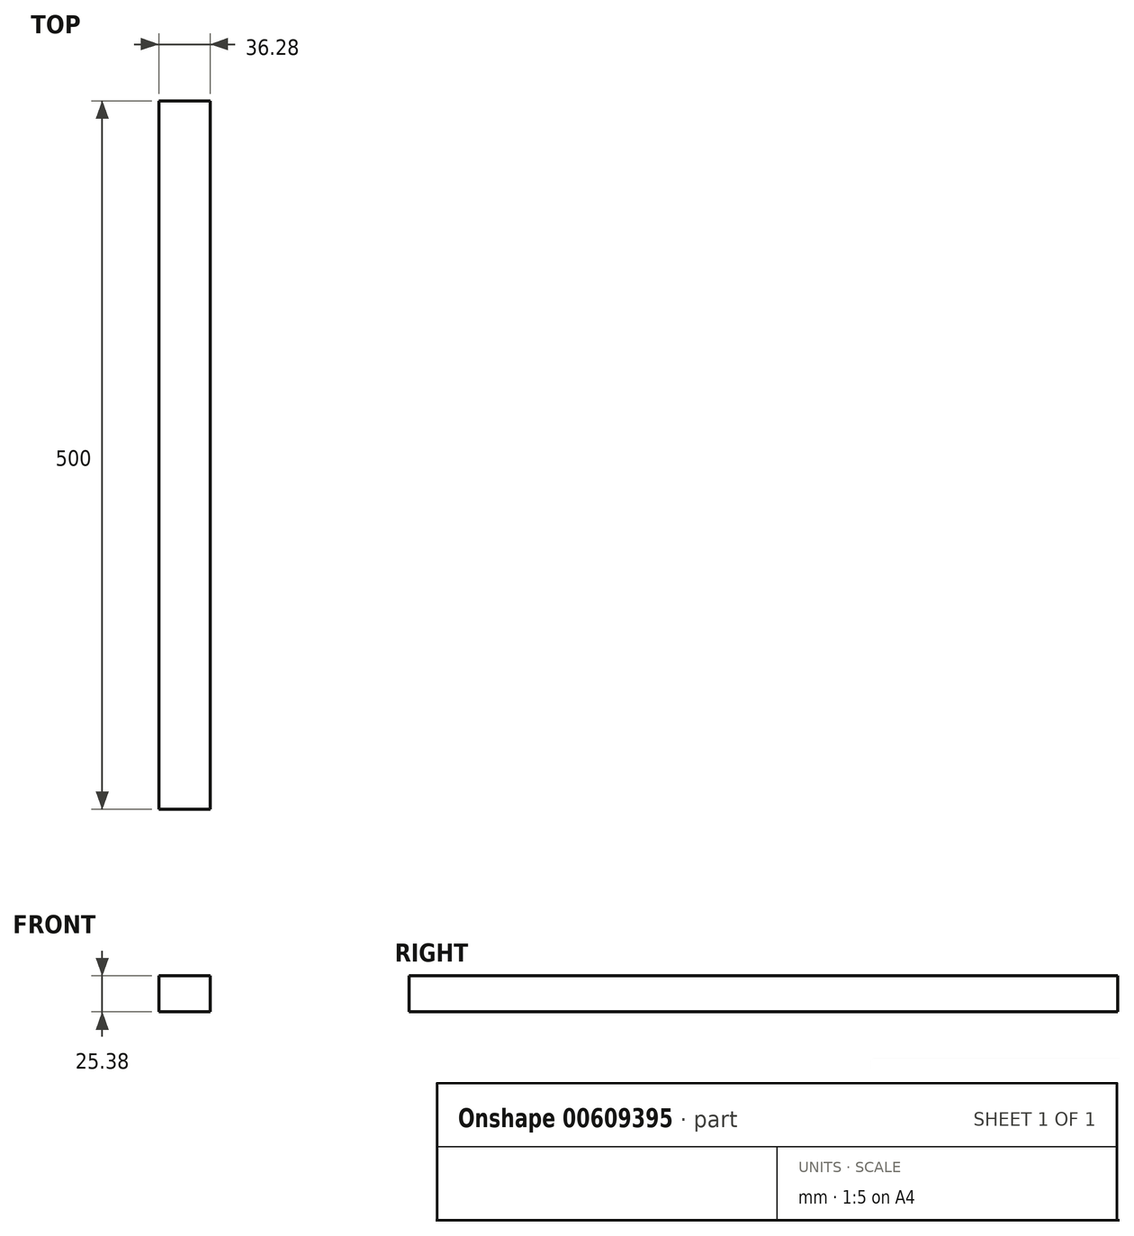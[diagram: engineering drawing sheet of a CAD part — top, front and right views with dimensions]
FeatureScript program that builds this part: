
annotation { "Feature Type Name" : "Feature", "Feature Type Description" : "" }
export const myFeature = defineFeature(function(context is Context, id is Id, definition is map)
    precondition{}
    {
        {
            var Q0;
            Q0=qCreatedBy(makeId("Front.planeOp"),FACE);
            var sketch = newSketch(context, id + "F0", { "sketchPlane" : qUnion([Q0])});
            skLineSegment(sketch, "E0.bottom", {"start": v(-36.28, 29.68) * mm, "end": v(0, 29.68) * mm});
            skLineSegment(sketch, "E0.top", {"start": v(-36.28, 4.3) * mm, "end": v(0, 4.3) * mm});
            skLineSegment(sketch, "E0.left", {"start": v(-36.28, 29.68) * mm, "end": v(-36.28, 4.3) * mm});
            skLineSegment(sketch, "E0.right", {"start": v(0, 29.68) * mm, "end": v(0, 4.3) * mm});
            skSolve(sketch);
        }
        {
            var Q0;
            Q0=makeQuery(id+"F0.imprint","IMPRINT",FACE,{"disambiguationData":[TD([[makeQuery(id+"F0.imprint","IMPRINT",EDGE,{"derivedFrom":sQuery(id+"F0.wireOp",EDGE,"E0.bottom")}),-1.0]])]});
            extrude(context, id + "F1", {"entities" : qUnion([Q0]), "depth" : 500 * mm, "offsetDistance" : 25 * mm});
        }
    });
